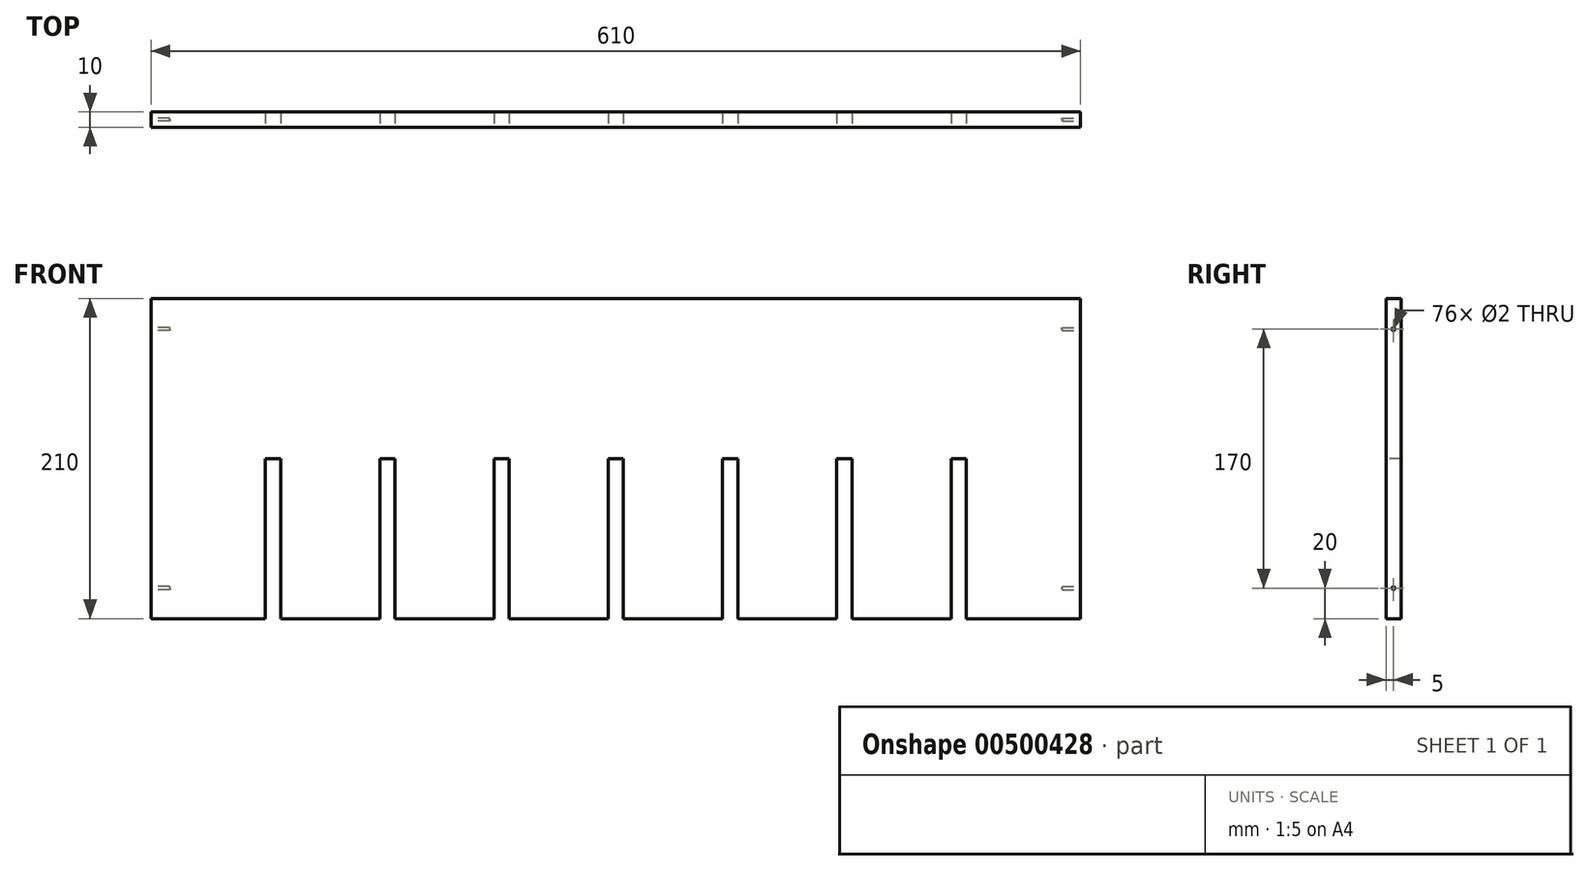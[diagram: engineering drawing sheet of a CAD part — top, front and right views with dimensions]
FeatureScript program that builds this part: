
annotation { "Feature Type Name" : "Feature", "Feature Type Description" : "" }
export const myFeature = defineFeature(function(context is Context, id is Id, definition is map)
    precondition{}
    {
        {
            var Q0;
            Q0=qCreatedBy(makeId("Front.planeOp"),FACE);
            var sketch = newSketch(context, id + "F0", { "sketchPlane" : qUnion([Q0])});
            skLineSegment(sketch, "E0.bottom", {"start": v(0, 0) * mm, "end": v(-610, 0) * mm});
            skLineSegment(sketch, "E0.top", {"start": v(0, 210) * mm, "end": v(-610, 210) * mm});
            skLineSegment(sketch, "E0.left", {"start": v(0, 0) * mm, "end": v(0, 210) * mm});
            skLineSegment(sketch, "E0.right", {"start": v(-610, 0) * mm, "end": v(-610, 210) * mm});
            skSolve(sketch);
        }
        {
            var Q0;
            Q0=makeQuery(id+"F0.imprint","IMPRINT",FACE,{"disambiguationData":[TD([[makeQuery(id+"F0.imprint","IMPRINT",EDGE,{"derivedFrom":sQuery(id+"F0.wireOp",EDGE,"E0.bottom")}),-1.0]])]});
            extrude(context, id + "F1", {"entities" : qUnion([Q0]), "depth" : 10 * mm});
        }
        {
            var Q0;
            Q0=makeQuery(id+"F1.opExtrude","CAP_FACE",FACE,{"disambiguationData":[OSD([sQuery(id+"F0.wireOp",EDGE,"E0.bottom"),sQuery(id+"F0.wireOp",EDGE,"E0.top"),sQuery(id+"F0.wireOp",EDGE,"E0.left"),sQuery(id+"F0.wireOp",EDGE,"E0.right")])],"isStart":false});
            var sketch = newSketch(context, id + "F2", { "sketchPlane" : qUnion([Q0])});
            skPoint(sketch, "E1", {"position": v(-535, 105) * mm});
            skPoint(sketch, "E2", {"position": v(-525, 105) * mm});
            skPoint(sketch, "E3", {"position": v(-460, 105) * mm});
            skPoint(sketch, "E4", {"position": v(-450, 105) * mm});
            skPoint(sketch, "E5", {"position": v(-385, 105) * mm});
            skPoint(sketch, "E6", {"position": v(-375, 105) * mm});
            skPoint(sketch, "E7", {"position": v(-310, 105) * mm});
            skPoint(sketch, "E8", {"position": v(-300, 105) * mm});
            skPoint(sketch, "E9", {"position": v(-235, 105) * mm});
            skPoint(sketch, "E10", {"position": v(-225, 105) * mm});
            skPoint(sketch, "E11", {"position": v(-160, 105) * mm});
            skPoint(sketch, "E12", {"position": v(-150, 105) * mm});
            skPoint(sketch, "E13", {"position": v(-85, 105) * mm});
            skPoint(sketch, "E14", {"position": v(-75, 105) * mm});
            skPoint(sketch, "E15", {"position": v(1213.9, 105) * mm});
            skPoint(sketch, "E16", {"position": v(1269.32, 105) * mm});
            skLineSegment(sketch, "E17.bottom", {"start": v(-535, 105) * mm, "end": v(-525, 105) * mm});
            skLineSegment(sketch, "E17.top", {"start": v(-535, 0) * mm, "end": v(-525, 0) * mm});
            skLineSegment(sketch, "E17.left", {"start": v(-535, 105) * mm, "end": v(-535, 0) * mm});
            skLineSegment(sketch, "E17.right", {"start": v(-525, 105) * mm, "end": v(-525, 0) * mm});
            skLineSegment(sketch, "E18.bottom", {"start": v(-460, 105) * mm, "end": v(-450, 105) * mm});
            skLineSegment(sketch, "E18.top", {"start": v(-460, 0) * mm, "end": v(-450, 0) * mm});
            skLineSegment(sketch, "E18.left", {"start": v(-460, 105) * mm, "end": v(-460, 0) * mm});
            skLineSegment(sketch, "E18.right", {"start": v(-450, 105) * mm, "end": v(-450, 0) * mm});
            skLineSegment(sketch, "E19.bottom", {"start": v(-385, 105) * mm, "end": v(-375, 105) * mm});
            skLineSegment(sketch, "E19.top", {"start": v(-385, 0) * mm, "end": v(-375, 0) * mm});
            skLineSegment(sketch, "E19.left", {"start": v(-385, 105) * mm, "end": v(-385, 0) * mm});
            skLineSegment(sketch, "E19.right", {"start": v(-375, 105) * mm, "end": v(-375, 0) * mm});
            skLineSegment(sketch, "E20.bottom", {"start": v(-310, 105) * mm, "end": v(-300, 105) * mm});
            skLineSegment(sketch, "E20.top", {"start": v(-310, 0) * mm, "end": v(-300, 0) * mm});
            skLineSegment(sketch, "E20.left", {"start": v(-310, 105) * mm, "end": v(-310, 0) * mm});
            skLineSegment(sketch, "E20.right", {"start": v(-300, 105) * mm, "end": v(-300, 0) * mm});
            skLineSegment(sketch, "E21.bottom", {"start": v(-235, 105) * mm, "end": v(-225, 105) * mm});
            skLineSegment(sketch, "E21.top", {"start": v(-235, 0) * mm, "end": v(-225, 0) * mm});
            skLineSegment(sketch, "E21.left", {"start": v(-235, 105) * mm, "end": v(-235, 0) * mm});
            skLineSegment(sketch, "E21.right", {"start": v(-225, 105) * mm, "end": v(-225, 0) * mm});
            skLineSegment(sketch, "E22.bottom", {"start": v(-160, 105) * mm, "end": v(-150, 105) * mm});
            skLineSegment(sketch, "E22.top", {"start": v(-160, 0) * mm, "end": v(-150, 0) * mm});
            skLineSegment(sketch, "E22.left", {"start": v(-160, 105) * mm, "end": v(-160, 0) * mm});
            skLineSegment(sketch, "E22.right", {"start": v(-150, 105) * mm, "end": v(-150, 0) * mm});
            skLineSegment(sketch, "E23.bottom", {"start": v(-85, 105) * mm, "end": v(-75, 105) * mm});
            skLineSegment(sketch, "E23.top", {"start": v(-85, 0) * mm, "end": v(-75, 0) * mm});
            skLineSegment(sketch, "E23.left", {"start": v(-85, 105) * mm, "end": v(-85, 0) * mm});
            skLineSegment(sketch, "E23.right", {"start": v(-75, 105) * mm, "end": v(-75, 0) * mm});
            skSolve(sketch);
        }
        {
            var Q0;
            Q0=makeQuery(id+"F2.imprint","IMPRINT",FACE,{"disambiguationData":[TD([[makeQuery(id+"F2.imprint","IMPRINT",EDGE,{"derivedFrom":sQuery(id+"F2.wireOp",EDGE,"E17.bottom")}),-1.0]])]});
            var Q1;
            Q1=makeQuery(id+"F2.imprint","IMPRINT",FACE,{"disambiguationData":[TD([[makeQuery(id+"F2.imprint","IMPRINT",EDGE,{"derivedFrom":sQuery(id+"F2.wireOp",EDGE,"E18.bottom")}),-1.0]])]});
            var Q2;
            Q2=makeQuery(id+"F2.imprint","IMPRINT",FACE,{"disambiguationData":[TD([[makeQuery(id+"F2.imprint","IMPRINT",EDGE,{"derivedFrom":sQuery(id+"F2.wireOp",EDGE,"E19.bottom")}),-1.0]])]});
            var Q3;
            Q3=makeQuery(id+"F2.imprint","IMPRINT",FACE,{"disambiguationData":[TD([[makeQuery(id+"F2.imprint","IMPRINT",EDGE,{"derivedFrom":sQuery(id+"F2.wireOp",EDGE,"E21.bottom")}),-1.0]])]});
            var Q4;
            Q4=makeQuery(id+"F2.imprint","IMPRINT",FACE,{"disambiguationData":[TD([[makeQuery(id+"F2.imprint","IMPRINT",EDGE,{"derivedFrom":sQuery(id+"F2.wireOp",EDGE,"E22.bottom")}),-1.0]])]});
            var Q5;
            Q5=makeQuery(id+"F2.imprint","IMPRINT",FACE,{"disambiguationData":[TD([[makeQuery(id+"F2.imprint","IMPRINT",EDGE,{"derivedFrom":sQuery(id+"F2.wireOp",EDGE,"E20.bottom")}),-1.0]])]});
            var Q6;
            Q6=makeQuery(id+"F2.imprint","IMPRINT",FACE,{"disambiguationData":[TD([[makeQuery(id+"F2.imprint","IMPRINT",EDGE,{"derivedFrom":sQuery(id+"F2.wireOp",EDGE,"E23.bottom")}),-1.0]])]});
            extrude(context, id + "F3", {"entities" : qUnion([Q0, Q1, Q2, Q3, Q4, Q5, Q6]), "operationType" : NewBodyOperationType.REMOVE, "oppositeDirection" : true, "depth" : 25 * mm});
        }
        {
            var Q0;
            Q0=makeQuery(id+"F1.opExtrude","SWEPT_FACE",FACE,{"disambiguationData":[OSD([sQuery(id+"F0.wireOp",EDGE,"E0.right")])]});
            var sketch = newSketch(context, id + "F4", { "sketchPlane" : qUnion([Q0])});
            skPoint(sketch, "E24", {"position": v(5, 190) * mm});
            skPoint(sketch, "E24.positionSnap0", {"position": v(5, 210) * mm});
            skPoint(sketch, "E25", {"position": v(5, 20) * mm});
            skSolve(sketch);
        }
        {
            var Q0;
            Q0=sQuery(id+"F4.wireOp",VERTEX,"E24");
            var Q1;
            Q1=sQuery(id+"F4.wireOp",VERTEX,"E25");
            var Q2;
            Q2=makeQuery(id+"F1.opExtrude","SWEPT_BODY",BODY,{"disambiguationData":[OSD([sQuery(id+"F0.wireOp",EDGE,"E0.bottom"),sQuery(id+"F0.wireOp",EDGE,"E0.top"),sQuery(id+"F0.wireOp",EDGE,"E0.left"),sQuery(id+"F0.wireOp",EDGE,"E0.right")])]});
            hole(context, id + "F5", {"style" : HoleStyle.SIMPLE, "endStyle" : HoleEndStyle.BLIND, "holeDiameter" : 2 * mm, "holeDepth" : 12 * mm, "isTappedThrough" : true, "tappedDepth" : 12 * mm, "tapClearance" : 3, "locations" : qUnion([Q0, Q1]), "scope" : qUnion([Q2])});
        }
        {
            var Q0;
            Q0=makeQuery(id+"F1.opExtrude","SWEPT_FACE",FACE,{"disambiguationData":[OSD([sQuery(id+"F0.wireOp",EDGE,"E0.left")])]});
            var sketch = newSketch(context, id + "F6", { "sketchPlane" : qUnion([Q0])});
            skPoint(sketch, "E26", {"position": v(-5, 190) * mm});
            skPoint(sketch, "E26.positionSnap0", {"position": v(-5, 210) * mm});
            skPoint(sketch, "E27", {"position": v(-5, 20) * mm});
            skSolve(sketch);
        }
        {
            var Q0;
            Q0=sQuery(id+"F6.wireOp",VERTEX,"E26");
            var Q1;
            Q1=sQuery(id+"F6.wireOp",VERTEX,"E27");
            var Q2;
            Q2=makeQuery(id+"F1.opExtrude","SWEPT_BODY",BODY,{"disambiguationData":[OSD([sQuery(id+"F0.wireOp",EDGE,"E0.bottom"),sQuery(id+"F0.wireOp",EDGE,"E0.top"),sQuery(id+"F0.wireOp",EDGE,"E0.left"),sQuery(id+"F0.wireOp",EDGE,"E0.right")])]});
            hole(context, id + "F7", {"style" : HoleStyle.SIMPLE, "endStyle" : HoleEndStyle.BLIND, "holeDiameter" : 2 * mm, "holeDepth" : 12 * mm, "isTappedThrough" : true, "tappedDepth" : 12 * mm, "tapClearance" : 3, "locations" : qUnion([Q0, Q1]), "scope" : qUnion([Q2])});
        }
    });
